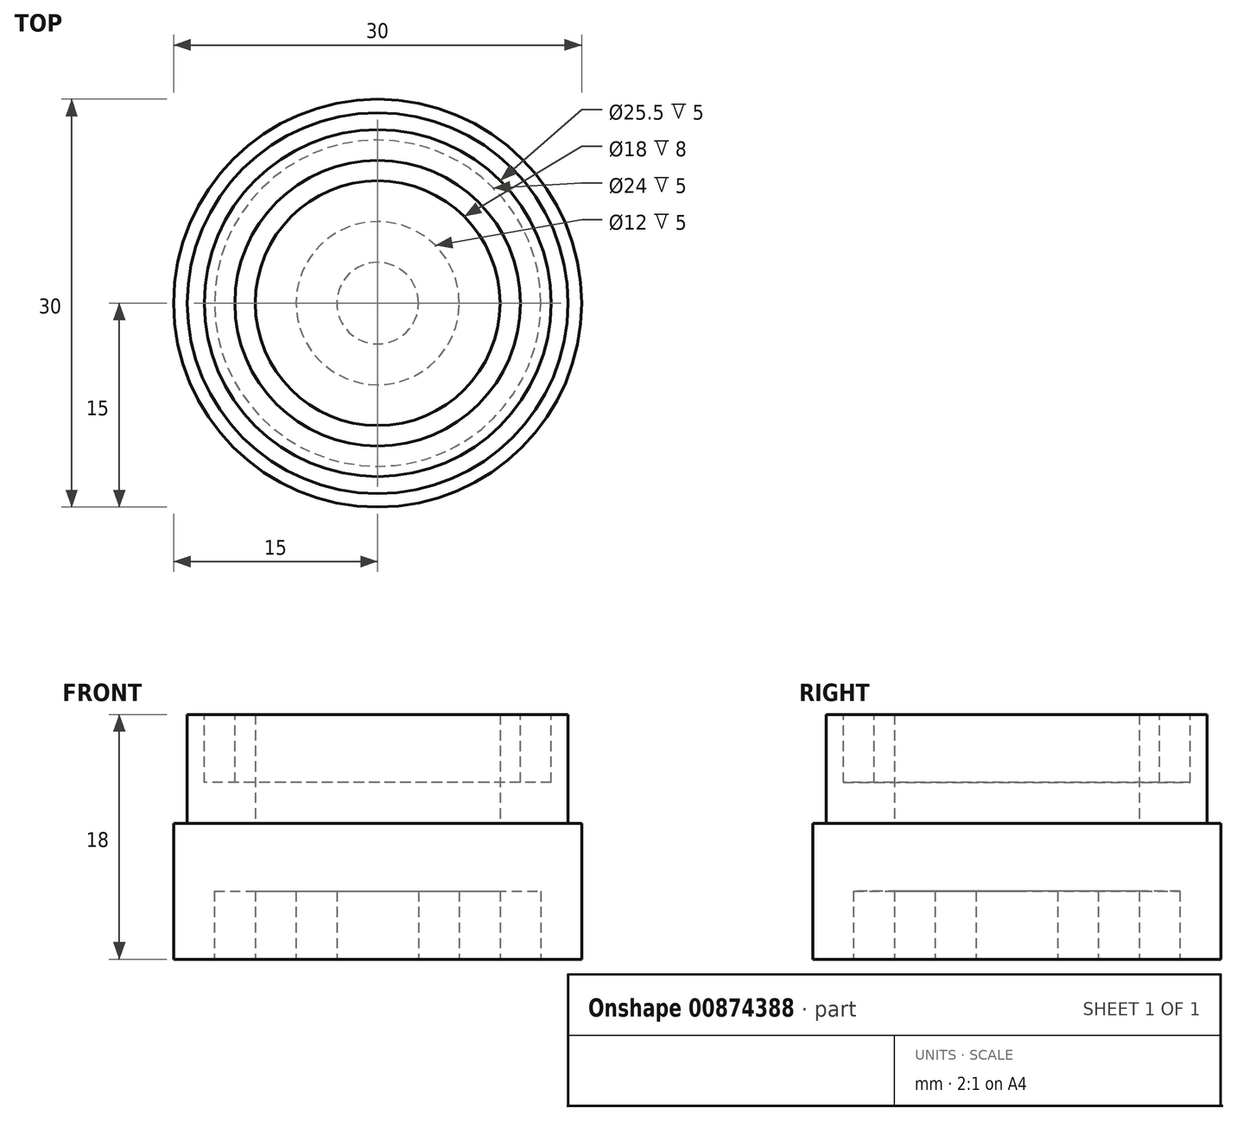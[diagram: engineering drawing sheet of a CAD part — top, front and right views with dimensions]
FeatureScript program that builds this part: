
annotation { "Feature Type Name" : "Feature", "Feature Type Description" : "" }
export const myFeature = defineFeature(function(context is Context, id is Id, definition is map)
    precondition{}
    {
        {
            var Q0;
            Q0=qCreatedBy(makeId("Top.planeOp"),FACE);
            var sketch = newSketch(context, id + "F0", { "sketchPlane" : qUnion([Q0])});
            skCircle(sketch, "E0", {"center": v(0, 0) * mm, "radius": 14 * mm});
            skCircle(sketch, "E1", {"center": v(0, 0) * mm, "radius": 9 * mm});
            skSolve(sketch);
        }
        {
            var Q0;
            Q0 = qSketchRegion(id + "F0", true);
            extrude(context, id + "F1", {"entities" : qUnion([Q0]), "depth" : 18 * mm, "offsetDistance" : 25 * mm});
        }
        {
            var Q0;
            Q0=makeQuery(id+"F1.opExtrude","CAP_FACE",FACE,{"disambiguationData":[OSD([sQuery(id+"F0.wireOp",EDGE,"E0"),sQuery(id+"F0.wireOp",EDGE,"E1")])],"isStart":true});
            var sketch = newSketch(context, id + "F2", { "sketchPlane" : qUnion([Q0])});
            skCircle(sketch, "E2", {"center": v(0, 0) * mm, "radius": 15 * mm});
            skSolve(sketch);
        }
        {
            var Q0;
            Q0 = qSketchRegion(id + "F2", true);
            extrude(context, id + "F3", {"entities" : qUnion([Q0]), "operationType" : NewBodyOperationType.ADD, "oppositeDirection" : true, "depth" : 10 * mm, "offsetDistance" : 25 * mm});
        }
        {
            var Q0;
            Q0=makeQuery(id+"F1.opExtrude","CAP_FACE",FACE,{"disambiguationData":[OSD([sQuery(id+"F0.wireOp",EDGE,"E0"),sQuery(id+"F0.wireOp",EDGE,"E1")])],"isStart":false});
            var sketch = newSketch(context, id + "F4", { "sketchPlane" : qUnion([Q0])});
            skCircle(sketch, "E3", {"center": v(0, 0) * mm, "radius": 12.75 * mm});
            skCircle(sketch, "E4", {"center": v(0, 0) * mm, "radius": 10.5 * mm});
            skSolve(sketch);
        }
        {
            var Q0;
            Q0 = qSketchRegion(id + "F4", true);
            extrude(context, id + "F5", {"entities" : qUnion([Q0]), "operationType" : NewBodyOperationType.REMOVE, "oppositeDirection" : true, "depth" : 5 * mm, "offsetDistance" : 25 * mm});
        }
        {
            var Q0;
            Q0=makeQuery(id+"F3.boolean.opBoolean","MERGE",FACE,{"derivedFrom":[makeQuery(id+"F1.opExtrude","CAP_FACE",FACE,{"disambiguationData":[OSD([sQuery(id+"F0.wireOp",EDGE,"E0"),sQuery(id+"F0.wireOp",EDGE,"E1")])],"isStart":true}),makeQuery(id+"F3.opExtrude","CAP_FACE",FACE,{"disambiguationData":[OSD([sQuery(id+"F2.wireOp",EDGE,"E2")])],"isStart":true})]});
            var sketch = newSketch(context, id + "F6", { "sketchPlane" : qUnion([Q0])});
            skCircle(sketch, "E5", {"center": v(0, 0) * mm, "radius": 3 * mm});
            skCircle(sketch, "E6", {"center": v(0, 0) * mm, "radius": 6 * mm});
            skSolve(sketch);
        }
        {
            var Q0;
            Q0 = qSketchRegion(id + "F6", true);
            extrude(context, id + "F7", {"entities" : qUnion([Q0]), "operationType" : NewBodyOperationType.REMOVE, "oppositeDirection" : true, "depth" : 5 * mm, "offsetDistance" : 25 * mm});
        }
        {
            var Q0;
            {var subQ0=sQuery(id+"F2.wireOp",EDGE,"E2");Q0=makeQuery(id+"F7.boolean.opBoolean","SPLIT",FACE,{"disambiguationData":[TD([makeQuery(id+"F3.opExtrude","SWEPT_FACE",FACE,{"disambiguationData":[OSD([subQ0])]})])],"derivedFrom":makeQuery(id+"F3.boolean.opBoolean","MERGE",FACE,{"derivedFrom":[makeQuery(id+"F1.opExtrude","CAP_FACE",FACE,{"disambiguationData":[OSD([sQuery(id+"F0.wireOp",EDGE,"E0"),sQuery(id+"F0.wireOp",EDGE,"E1")])],"isStart":true}),makeQuery(id+"F3.opExtrude","CAP_FACE",FACE,{"disambiguationData":[OSD([subQ0])],"isStart":true})]})});}
            var sketch = newSketch(context, id + "F8", { "sketchPlane" : qUnion([Q0])});
            skCircle(sketch, "E7", {"center": v(0, 0) * mm, "radius": 9 * mm});
            skCircle(sketch, "E8", {"center": v(0, 0) * mm, "radius": 12 * mm});
            skSolve(sketch);
        }
        {
            var Q0;
            Q0 = qSketchRegion(id + "F8", true);
            extrude(context, id + "F9", {"entities" : qUnion([Q0]), "operationType" : NewBodyOperationType.REMOVE, "oppositeDirection" : true, "depth" : 5 * mm, "offsetDistance" : 25 * mm});
        }
    });
